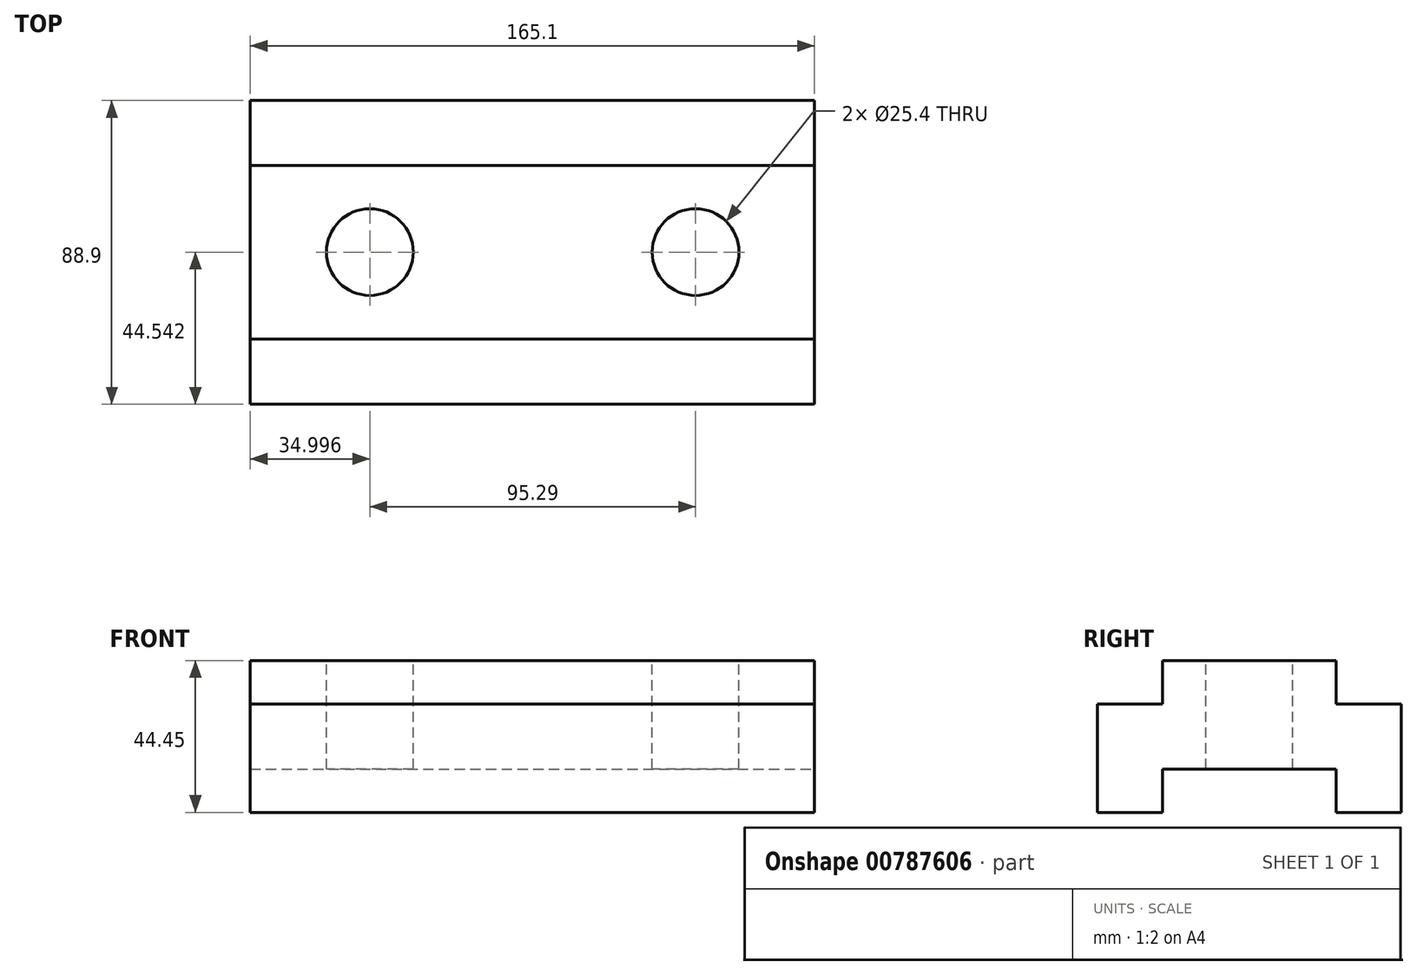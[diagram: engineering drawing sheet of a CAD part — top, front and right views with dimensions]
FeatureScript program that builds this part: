
annotation { "Feature Type Name" : "Feature", "Feature Type Description" : "" }
export const myFeature = defineFeature(function(context is Context, id is Id, definition is map)
    precondition{}
    {
        {
            var Q0;
            Q0=qCreatedBy(makeId("Front.planeOp"),FACE);
            var sketch = newSketch(context, id + "F0", { "sketchPlane" : qUnion([Q0])});
            skLineSegment(sketch, "E0", {"start": v(0, 0) * mm, "end": v(165.1, 0) * mm});
            skLineSegment(sketch, "E1", {"start": v(165.1, 0) * mm, "end": v(165.1, 44.45) * mm});
            skLineSegment(sketch, "E2", {"start": v(0, 44.45) * mm, "end": v(0, 0) * mm});
            skLineSegment(sketch, "E3", {"start": v(165.1, 44.45) * mm, "end": v(0, 44.45) * mm});
            skSolve(sketch);
        }
        {
            var Q0;
            Q0 = qSketchRegion(id + "F0", true);
            extrude(context, id + "F1", {"entities" : qUnion([Q0]), "depth" : 88.9 * mm, "offsetDistance" : 25.4 * mm});
        }
        {
            var Q0;
            Q0=makeQuery(id+"F1.opExtrude","SWEPT_FACE",FACE,{"disambiguationData":[OSD([sQuery(id+"F0.wireOp",EDGE,"E1")])]});
            var sketch = newSketch(context, id + "F2", { "sketchPlane" : qUnion([Q0])});
            skLineSegment(sketch, "E4", {"start": v(-88.9, 44.45) * mm, "end": v(-69.85, 44.45) * mm});
            skLineSegment(sketch, "E5", {"start": v(-69.85, 44.45) * mm, "end": v(-69.85, 31.75) * mm});
            skLineSegment(sketch, "E6", {"start": v(-69.85, 31.75) * mm, "end": v(-88.9, 31.75) * mm});
            skLineSegment(sketch, "E7", {"start": v(-88.9, 31.75) * mm, "end": v(-88.9, 44.45) * mm});
            skSolve(sketch);
        }
        {
            var Q0;
            Q0 = qSketchRegion(id + "F2", true);
            extrude(context, id + "F3", {"entities" : qUnion([Q0]), "operationType" : NewBodyOperationType.REMOVE, "endBound" : BoundingType.THROUGH_ALL, "oppositeDirection" : true, "depth" : 25.4 * mm, "offsetDistance" : 25.4 * mm});
        }
        {
            var Q0;
            Q0=makeQuery(id+"F1.opExtrude","SWEPT_FACE",FACE,{"disambiguationData":[OSD([sQuery(id+"F0.wireOp",EDGE,"E1")])]});
            var sketch = newSketch(context, id + "F4", { "sketchPlane" : qUnion([Q0])});
            skLineSegment(sketch, "E8", {"start": v(0, 44.45) * mm, "end": v(-19.05, 44.45) * mm});
            skLineSegment(sketch, "E9", {"start": v(-19.05, 44.45) * mm, "end": v(-19.05, 31.75) * mm});
            skLineSegment(sketch, "E10", {"start": v(-19.05, 31.75) * mm, "end": v(0, 31.75) * mm});
            skLineSegment(sketch, "E11", {"start": v(0, 31.75) * mm, "end": v(0, 44.45) * mm});
            skSolve(sketch);
        }
        {
            var Q0;
            Q0 = qSketchRegion(id + "F4", true);
            extrude(context, id + "F5", {"entities" : qUnion([Q0]), "operationType" : NewBodyOperationType.REMOVE, "endBound" : BoundingType.THROUGH_ALL, "oppositeDirection" : true, "depth" : 25.4 * mm, "offsetDistance" : 25.4 * mm});
        }
        {
            var Q0;
            Q0=makeQuery(id+"F1.opExtrude","SWEPT_FACE",FACE,{"disambiguationData":[OSD([sQuery(id+"F0.wireOp",EDGE,"E1")])]});
            var sketch = newSketch(context, id + "F6", { "sketchPlane" : qUnion([Q0])});
            skLineSegment(sketch, "E12", {"start": v(-44.45, 0) * mm, "end": v(-19.05, 0) * mm});
            skLineSegment(sketch, "E13", {"start": v(-19.05, 0) * mm, "end": v(-19.05, 12.7) * mm});
            skLineSegment(sketch, "E14", {"start": v(-19.05, 12.7) * mm, "end": v(-69.85, 12.7) * mm});
            skLineSegment(sketch, "E15", {"start": v(-69.85, 12.7) * mm, "end": v(-69.85, 0) * mm});
            skLineSegment(sketch, "E16", {"start": v(-69.85, 0) * mm, "end": v(-44.45, 0) * mm});
            skSolve(sketch);
        }
        {
            var Q0;
            Q0 = qSketchRegion(id + "F6", true);
            extrude(context, id + "F7", {"entities" : qUnion([Q0]), "operationType" : NewBodyOperationType.REMOVE, "endBound" : BoundingType.THROUGH_ALL, "oppositeDirection" : true, "depth" : 25.4 * mm, "offsetDistance" : 25.4 * mm});
        }
        {
            var Q0;
            Q0=makeQuery(id+"F1.opExtrude","SWEPT_FACE",FACE,{"disambiguationData":[OSD([sQuery(id+"F0.wireOp",EDGE,"E3")])]});
            var sketch = newSketch(context, id + "F8", { "sketchPlane" : qUnion([Q0])});
            skLineSegment(sketch, "E17", {"start": v(0, -44.45) * mm, "end": v(34.93, -44.45) * mm, "construction": true});
            skLineSegment(sketch, "E18", {"start": v(34.93, -44.45) * mm, "end": v(130.18, -44.45) * mm, "construction": true});
            skSolve(sketch);
        }
        {
            var Q0;
            {var subQ0=sQuery(id+"F0.wireOp",EDGE,"E3");var subQ1=sQuery(id+"F0.wireOp",EDGE,"E1");Q0=makeQuery(id+"F8.imprint","IMPRINT",FACE,{"disambiguationData":[TD([[makeQuery(id+"F8.imprint","IMPRINT",EDGE,{"derivedFrom":makeQuery(id+"F1.opExtrude","SWEPT_EDGE",EDGE,{"disambiguationData":[OSD([subQ1,subQ0])]})}),1.0]])]});}
            var sketch = newSketch(context, id + "F9", { "sketchPlane" : qUnion([Q0])});
            skCircle(sketch, "E19", {"center": v(35, -44.36) * mm, "radius": 12.7 * mm});
            skCircle(sketch, "E20", {"center": v(130.29, -44.36) * mm, "radius": 12.7 * mm});
            skSolve(sketch);
        }
        {
            var Q0;
            Q0 = qSketchRegion(id + "F9", true);
            extrude(context, id + "F10", {"entities" : qUnion([Q0]), "operationType" : NewBodyOperationType.REMOVE, "endBound" : BoundingType.THROUGH_ALL, "oppositeDirection" : true, "depth" : 25.4 * mm, "offsetDistance" : 25.4 * mm});
        }
    });
